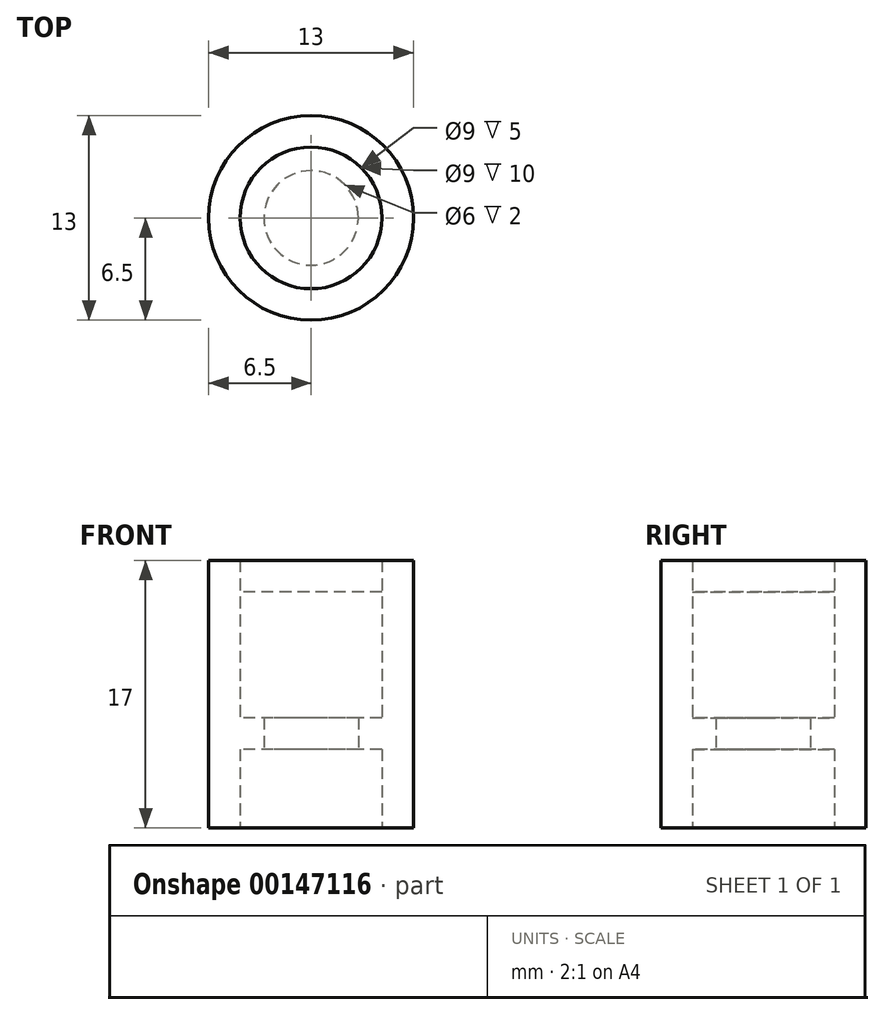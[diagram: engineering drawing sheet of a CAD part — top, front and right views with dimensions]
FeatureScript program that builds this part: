
annotation { "Feature Type Name" : "Feature", "Feature Type Description" : "" }
export const myFeature = defineFeature(function(context is Context, id is Id, definition is map)
    precondition{}
    {
        {
            var Q0;
            Q0=qCreatedBy(makeId("Top.planeOp"),FACE);
            var sketch = newSketch(context, id + "F0", { "sketchPlane" : qUnion([Q0])});
            skCircle(sketch, "E0", {"center": v(0, 0) * mm, "radius": 4.5 * mm});
            skCircle(sketch, "E1", {"center": v(0, 0) * mm, "radius": 6.5 * mm});
            skCircle(sketch, "E2", {"center": v(0, 0) * mm, "radius": 3 * mm});
            skSolve(sketch);
        }
        {
            var Q0;
            Q0 = qSketchRegion(id + "F0", true);
            extrude(context, id + "F1", {"entities" : qUnion([Q0]), "depth" : 17 * mm});
        }
        {
            var Q0;
            Q0=makeQuery(id+"F0.imprint","IMPRINT",FACE,{"disambiguationData":[TD([[makeQuery(id+"F0.imprint","IMPRINT",EDGE,{"derivedFrom":sQuery(id+"F0.wireOp",EDGE,"E0")}),1.0]])]});
            extrude(context, id + "F2", {"entities" : qUnion([Q0]), "operationType" : NewBodyOperationType.ADD, "depth" : 7 * mm, "hasSecondDirection" : true, "secondDirectionOppositeDirection" : false, "secondDirectionDepth" : 5 * mm});
        }
        {
            var Q0;
            Q0=makeQuery(id+"F0.imprint","IMPRINT",FACE,{"disambiguationData":[TD([[makeQuery(id+"F0.imprint","IMPRINT",EDGE,{"derivedFrom":sQuery(id+"F0.wireOp",EDGE,"E2")}),1.0]])]});
            var Q1;
            Q1=makeQuery(id+"F0.imprint","IMPRINT",FACE,{"disambiguationData":[TD([[makeQuery(id+"F0.imprint","IMPRINT",EDGE,{"derivedFrom":sQuery(id+"F0.wireOp",EDGE,"E0")}),1.0]])]});
            extrude(context, id + "F3", {"entities" : qUnion([Q0, Q1]), "depth" : 17 * mm, "hasSecondDirection" : true, "secondDirectionOppositeDirection" : false, "secondDirectionDepth" : 15 * mm});
        }
    });
